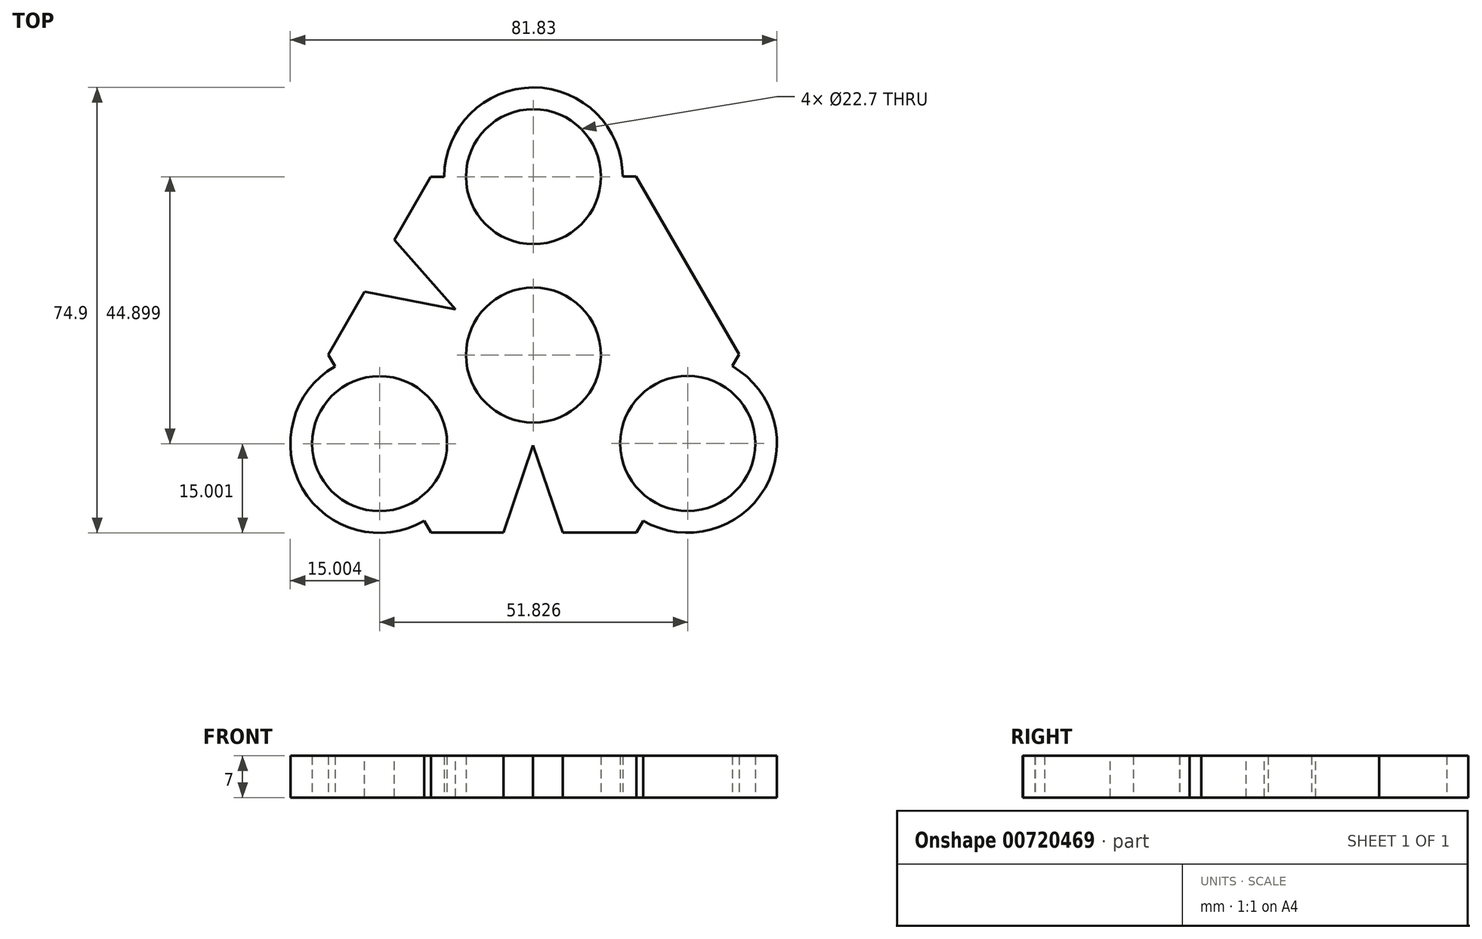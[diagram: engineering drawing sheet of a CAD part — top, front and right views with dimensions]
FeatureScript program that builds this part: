
annotation { "Feature Type Name" : "Feature", "Feature Type Description" : "" }
export const myFeature = defineFeature(function(context is Context, id is Id, definition is map)
    precondition{}
    {
        {
            var Q0;
            Q0=qCreatedBy(makeId("Top.planeOp"),FACE);
            var sketch = newSketch(context, id + "F0", { "sketchPlane" : qUnion([Q0])});
            skCircle(sketch, "E0", {"center": v(0, 0) * mm, "radius": 281.06 * mm});
            skCircle(sketch, "E1", {"center": v(0, 0) * mm, "radius": 11.35 * mm});
            skCircle(sketch, "E2", {"center": v(0, 30) * mm, "radius": 11.35 * mm});
            skCircle(sketch, "E3", {"center": v(0, 30) * mm, "radius": 15 * mm});
            skCircle(sketch, "E4.1.0", {"center": v(-25.89, -14.9) * mm, "radius": 11.35 * mm});
            skCircle(sketch, "E4.1.1", {"center": v(-25.89, -14.9) * mm, "radius": 15 * mm});
            skCircle(sketch, "E4.2.0", {"center": v(25.94, -14.87) * mm, "radius": 11.35 * mm});
            skCircle(sketch, "E4.2.1", {"center": v(25.94, -14.87) * mm, "radius": 15 * mm});
            skPoint(sketch, "E4.center", {"position": v(0.02, 0.08) * mm});
            skLineSegment(sketch, "E5.0", {"start": v(-17.28, 29.99) * mm, "end": v(17.28, 30.01) * mm});
            skLineSegment(sketch, "E5.1", {"start": v(17.28, 30.01) * mm, "end": v(34.57, 0.1) * mm});
            skLineSegment(sketch, "E5.2", {"start": v(34.57, 0.1) * mm, "end": v(17.31, -29.83) * mm});
            skLineSegment(sketch, "E5.3", {"start": v(17.31, -29.83) * mm, "end": v(-17.24, -29.85) * mm});
            skLineSegment(sketch, "E5.4", {"start": v(-17.24, -29.85) * mm, "end": v(-34.53, 0.06) * mm});
            skLineSegment(sketch, "E5.5", {"start": v(-34.53, 0.06) * mm, "end": v(-17.28, 29.99) * mm});
            skSolve(sketch);
        }
        {
            var Q0;
            Q0=makeQuery(id+"F0.imprint","IMPRINT",FACE,{"disambiguationData":[TD([[makeQuery(id+"F0.imprint","IMPRINT",EDGE,{"derivedFrom":sQuery(id+"F0.wireOp",EDGE,"E4.1.0")}),-1.0]])]});
            var Q1;
            Q1=makeQuery(id+"F0.imprint","IMPRINT",FACE,{"disambiguationData":[TD([[makeQuery(id+"F0.imprint","IMPRINT",EDGE,{"derivedFrom":sQuery(id+"F0.wireOp",EDGE,"E2")}),-1.0]])]});
            var Q2;
            Q2=makeQuery(id+"F0.imprint","IMPRINT",FACE,{"disambiguationData":[TD([[makeQuery(id+"F0.imprint","IMPRINT",EDGE,{"derivedFrom":sQuery(id+"F0.wireOp",EDGE,"E4.4.0")}),-1.0]])]});
            var Q3;
            Q3=makeQuery(id+"F0.imprint","IMPRINT",FACE,{"disambiguationData":[TD([[makeQuery(id+"F0.imprint","IMPRINT",EDGE,{"derivedFrom":sQuery(id+"F0.wireOp",EDGE,"E4.3.0")}),-1.0]])]});
            var Q4;
            Q4=makeQuery(id+"F0.imprint","IMPRINT",FACE,{"disambiguationData":[TD([[makeQuery(id+"F0.imprint","IMPRINT",EDGE,{"derivedFrom":sQuery(id+"F0.wireOp",EDGE,"E4.2.0")}),-1.0]])]});
            var Q5;
            Q5=makeQuery(id+"F0.imprint","IMPRINT",FACE,{"disambiguationData":[TD([[makeQuery(id+"F0.imprint","IMPRINT",EDGE,{"derivedFrom":sQuery(id+"F0.wireOp",EDGE,"E1")}),-1.0]])]});
            extrude(context, id + "F1", {"entities" : qUnion([Q0, Q1, Q2, Q3, Q4, Q5]), "depth" : 7 * mm, "offsetDistance" : 25 * mm});
        }
        {
            var Q0;
            Q0=makeQuery(id+"F1.opExtrude","CAP_FACE",FACE,{"disambiguationData":[OSD([sQuery(id+"F0.wireOp",EDGE,"E1"),sQuery(id+"F0.wireOp",EDGE,"E2"),sQuery(id+"F0.wireOp",EDGE,"E3"),sQuery(id+"F0.wireOp",EDGE,"E4.1.0"),sQuery(id+"F0.wireOp",EDGE,"E4.1.1"),sQuery(id+"F0.wireOp",EDGE,"E4.2.0"),sQuery(id+"F0.wireOp",EDGE,"E4.2.1"),sQuery(id+"F0.wireOp",EDGE,"E5.0"),sQuery(id+"F0.wireOp",EDGE,"E5.1"),sQuery(id+"F0.wireOp",EDGE,"E5.2"),sQuery(id+"F0.wireOp",EDGE,"E5.3"),sQuery(id+"F0.wireOp",EDGE,"E5.4"),sQuery(id+"F0.wireOp",EDGE,"E5.5")])],"isStart":false});
            var sketch = newSketch(context, id + "F2", { "sketchPlane" : qUnion([Q0])});
            skLineSegment(sketch, "E6", {"start": v(-23.4, 19.35) * mm, "end": v(-13.12, 7.65) * mm});
            skLineSegment(sketch, "E7", {"start": v(-13.12, 7.65) * mm, "end": v(-28.4, 10.7) * mm});
            skLineSegment(sketch, "E8.1.0", {"start": v(-5.06, -29.95) * mm, "end": v(-0.07, -15.2) * mm});
            skLineSegment(sketch, "E8.1.1", {"start": v(-0.07, -15.2) * mm, "end": v(4.94, -29.94) * mm});
            skLineSegment(sketch, "E8.2.0", {"start": v(28.47, 10.6) * mm, "end": v(13.19, 7.54) * mm});
            skLineSegment(sketch, "E8.2.1", {"start": v(13.19, 7.54) * mm, "end": v(23.46, 19.25) * mm});
            skPoint(sketch, "E8.center", {"position": v(0, 0) * mm});
            skSolve(sketch);
        }
        {
            var Q0;
            Q0 = qSketchRegion(id + "F2", true);
            var Q1;
            {var subQ0=sQuery(id+"F2.wireOp",EDGE,"E6");Q1=makeQuery(id+"F2.imprint","IMPRINT",FACE,{"disambiguationData":[TD([[makeQuery(id+"F2.imprint","IMPRINT",EDGE,{"derivedFrom":subQ0}),-1.0]])]});}
            var Q2;
            {var subQ0=sQuery(id+"F2.wireOp",EDGE,"E8.1.1");var subQ1=sQuery(id+"F2.wireOp",EDGE,"E8.1.0");var subQ2=makeQuery(id+"F2.imprint","INTERSECT",VERTEX,{"derivedFrom":[subQ1,subQ0]});Q2=makeQuery(id+"F2.imprint","IMPRINT",FACE,{"disambiguationData":[TD([[makeQuery(id+"F2.imprint","IMPRINT",EDGE,{"disambiguationData":[TD([[subQ2,1.0]])],"derivedFrom":subQ1}),-1.0]])]});}
            extrude(context, id + "F3", {"entities" : qUnion([Q0, Q1, Q2]), "operationType" : NewBodyOperationType.REMOVE, "oppositeDirection" : true, "depth" : 50.7 * mm, "offsetDistance" : 25 * mm});
        }
    });
